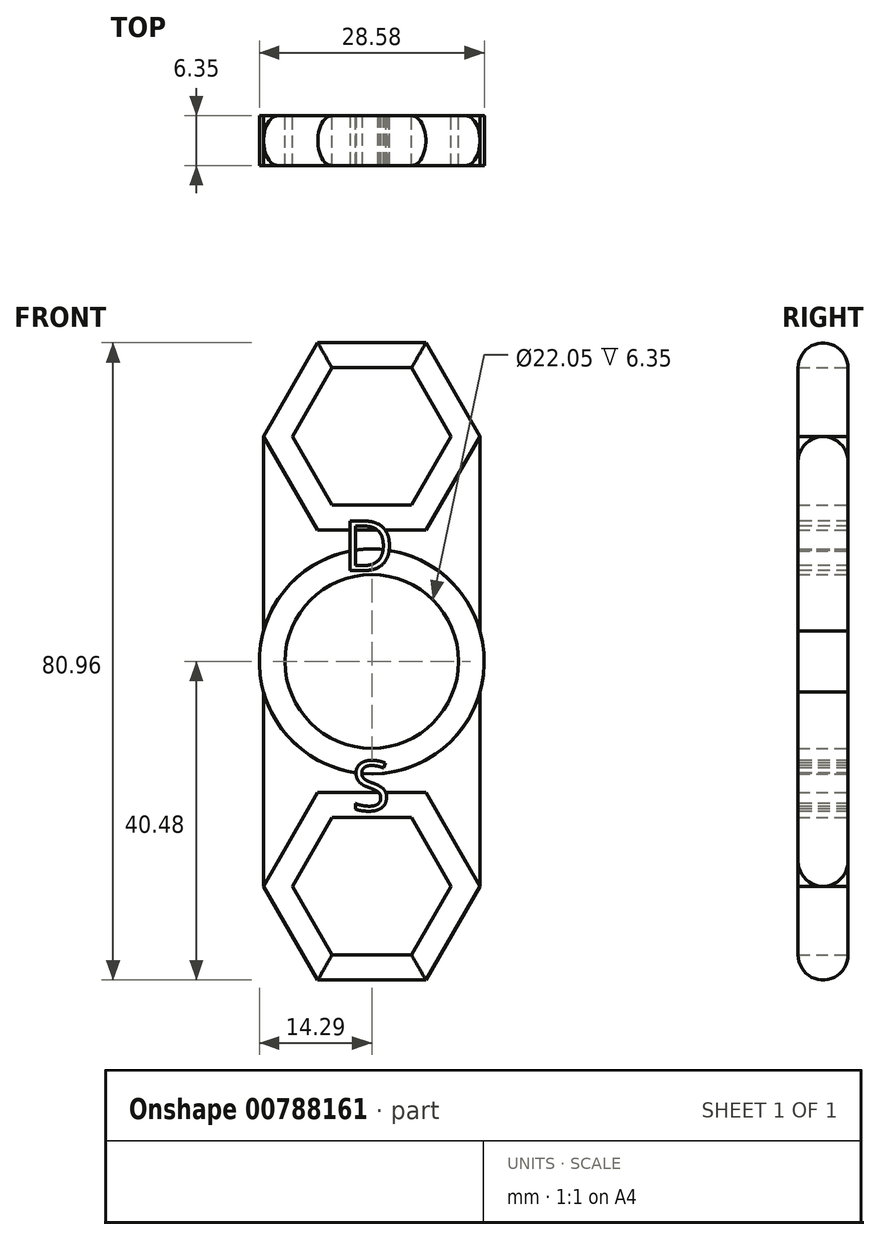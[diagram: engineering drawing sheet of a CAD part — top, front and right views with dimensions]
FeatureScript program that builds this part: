
annotation { "Feature Type Name" : "Feature", "Feature Type Description" : "" }
export const myFeature = defineFeature(function(context is Context, id is Id, definition is map)
    precondition{}
    {
        {
            var Q0;
            Q0=qCreatedBy(makeId("Front.planeOp"),FACE);
            var sketch = newSketch(context, id + "F0", { "sketchPlane" : qUnion([Q0])});
            skCircle(sketch, "E0", {"center": v(0, 0) * mm, "radius": 11.02 * mm});
            skCircle(sketch, "E1", {"center": v(0, 0) * mm, "radius": 14.29 * mm});
            skCircle(sketch, "E2.cCircle", {"center": v(0, 28.58) * mm, "radius": 8.73 * mm, "construction": true});
            skLineSegment(sketch, "E2.0", {"start": v(-5.04, 37.3) * mm, "end": v(5.04, 37.3) * mm});
            skLineSegment(sketch, "E2.1", {"start": v(5.04, 37.3) * mm, "end": v(10.08, 28.58) * mm});
            skLineSegment(sketch, "E2.2", {"start": v(10.08, 28.58) * mm, "end": v(5.04, 19.84) * mm});
            skLineSegment(sketch, "E2.3", {"start": v(5.04, 19.84) * mm, "end": v(-5.04, 19.84) * mm});
            skLineSegment(sketch, "E2.4", {"start": v(-5.04, 19.84) * mm, "end": v(-10.08, 28.58) * mm});
            skLineSegment(sketch, "E2.5", {"start": v(-10.08, 28.57) * mm, "end": v(-5.04, 37.3) * mm});
            skPoint(sketch, "E2.0.midPoint", {"position": v(0, 37.3) * mm});
            skCircle(sketch, "E3.cCircle", {"center": v(0, 28.58) * mm, "radius": 11.9 * mm, "construction": true});
            skLineSegment(sketch, "E3.0", {"start": v(-13.75, 28.58) * mm, "end": v(-6.87, 40.48) * mm});
            skLineSegment(sketch, "E3.1", {"start": v(-6.87, 40.48) * mm, "end": v(6.87, 40.48) * mm});
            skLineSegment(sketch, "E3.2", {"start": v(6.87, 40.48) * mm, "end": v(13.75, 28.58) * mm});
            skLineSegment(sketch, "E3.3", {"start": v(13.75, 28.58) * mm, "end": v(6.87, 16.67) * mm});
            skLineSegment(sketch, "E3.4", {"start": v(6.87, 16.67) * mm, "end": v(-6.87, 16.67) * mm});
            skLineSegment(sketch, "E3.5", {"start": v(-6.87, 16.67) * mm, "end": v(-13.75, 28.58) * mm});
            skPoint(sketch, "E3.0.midPoint", {"position": v(-10.31, 34.53) * mm});
            skCircle(sketch, "E4.1.0", {"center": v(0, -28.58) * mm, "radius": 11.9 * mm, "construction": true});
            skPoint(sketch, "E4.1.1", {"position": v(0, -37.3) * mm});
            skCircle(sketch, "E4.1.2", {"center": v(0, -28.58) * mm, "radius": 8.73 * mm, "construction": true});
            skPoint(sketch, "E4.1.3", {"position": v(10.31, -34.53) * mm});
            skLineSegment(sketch, "E4.1.4", {"start": v(-6.87, -16.67) * mm, "end": v(6.87, -16.67) * mm});
            skLineSegment(sketch, "E4.1.5", {"start": v(-5.04, -19.84) * mm, "end": v(5.04, -19.84) * mm});
            skLineSegment(sketch, "E4.1.6", {"start": v(-10.08, -28.58) * mm, "end": v(-5.04, -19.84) * mm});
            skLineSegment(sketch, "E4.1.7", {"start": v(5.04, -19.84) * mm, "end": v(10.08, -28.58) * mm});
            skLineSegment(sketch, "E4.1.8", {"start": v(10.08, -28.57) * mm, "end": v(5.04, -37.3) * mm});
            skLineSegment(sketch, "E4.1.9", {"start": v(5.04, -37.3) * mm, "end": v(-5.04, -37.3) * mm});
            skLineSegment(sketch, "E4.1.10", {"start": v(13.75, -28.58) * mm, "end": v(6.87, -40.48) * mm});
            skLineSegment(sketch, "E4.1.11", {"start": v(6.87, -40.48) * mm, "end": v(-6.87, -40.48) * mm});
            skLineSegment(sketch, "E4.1.12", {"start": v(-6.87, -40.48) * mm, "end": v(-13.75, -28.57) * mm});
            skLineSegment(sketch, "E4.1.13", {"start": v(-5.04, -37.3) * mm, "end": v(-10.08, -28.57) * mm});
            skLineSegment(sketch, "E4.1.14", {"start": v(6.87, -16.67) * mm, "end": v(13.75, -28.58) * mm});
            skLineSegment(sketch, "E4.1.15", {"start": v(-13.75, -28.58) * mm, "end": v(-6.87, -16.67) * mm});
            skSolve(sketch);
        }
        {
            var Q0;
            Q0=qCreatedBy(makeId("Front.planeOp"),FACE);
            var sketch = newSketch(context, id + "F1", { "sketchPlane" : qUnion([Q0])});
            skLineSegment(sketch, "E5.0", {"start": v(13.75, 28.58) * mm, "end": v(6.87, 16.67) * mm});
            skLineSegment(sketch, "E5.1", {"start": v(-5.04, -19.84) * mm, "end": v(5.04, -19.84) * mm});
            skLineSegment(sketch, "E5.2", {"start": v(5.04, -19.84) * mm, "end": v(10.08, -28.58) * mm});
            skLineSegment(sketch, "E5.3", {"start": v(13.75, -28.58) * mm, "end": v(6.87, -40.48) * mm});
            skLineSegment(sketch, "E5.4", {"start": v(-6.87, -40.48) * mm, "end": v(-13.75, -28.57) * mm});
            skLineSegment(sketch, "E5.5", {"start": v(6.87, -16.67) * mm, "end": v(13.75, -28.58) * mm});
            skLineSegment(sketch, "E5.6", {"start": v(6.87, 16.67) * mm, "end": v(-6.87, 16.67) * mm});
            skCircle(sketch, "E5.7", {"center": v(0, -28.58) * mm, "radius": 8.73 * mm});
            skLineSegment(sketch, "E5.8", {"start": v(-6.87, 16.67) * mm, "end": v(-13.75, 28.58) * mm});
            skCircle(sketch, "E5.9", {"center": v(0, 0) * mm, "radius": 11.02 * mm});
            skCircle(sketch, "E5.10", {"center": v(0, 0) * mm, "radius": 14.29 * mm});
            skCircle(sketch, "E5.11", {"center": v(0, 28.58) * mm, "radius": 8.73 * mm});
            skLineSegment(sketch, "E5.12", {"start": v(5.04, 37.3) * mm, "end": v(10.08, 28.58) * mm});
            skLineSegment(sketch, "E5.13", {"start": v(10.08, 28.58) * mm, "end": v(5.04, 19.84) * mm});
            skLineSegment(sketch, "E5.14", {"start": v(5.04, 19.84) * mm, "end": v(-5.04, 19.84) * mm});
            skLineSegment(sketch, "E5.15", {"start": v(-5.04, 19.84) * mm, "end": v(-10.08, 28.58) * mm});
            skLineSegment(sketch, "E5.16", {"start": v(-10.08, 28.57) * mm, "end": v(-5.04, 37.3) * mm});
            skCircle(sketch, "E5.17", {"center": v(0, 28.58) * mm, "radius": 11.9 * mm});
            skLineSegment(sketch, "E5.18", {"start": v(-13.75, 28.58) * mm, "end": v(-6.87, 40.48) * mm});
            skLineSegment(sketch, "E5.19", {"start": v(-6.87, 40.48) * mm, "end": v(6.87, 40.48) * mm});
            skLineSegment(sketch, "E5.20", {"start": v(6.87, 40.48) * mm, "end": v(13.75, 28.58) * mm});
            skLineSegment(sketch, "E5.21", {"start": v(-5.04, -37.3) * mm, "end": v(-10.08, -28.58) * mm});
            skLineSegment(sketch, "E5.22", {"start": v(6.87, -40.48) * mm, "end": v(-6.87, -40.48) * mm});
            skLineSegment(sketch, "E5.23", {"start": v(10.08, -28.57) * mm, "end": v(5.04, -37.3) * mm});
            skLineSegment(sketch, "E5.24", {"start": v(-10.08, -28.58) * mm, "end": v(-5.04, -19.84) * mm});
            skLineSegment(sketch, "E5.25", {"start": v(-13.75, -28.58) * mm, "end": v(-6.87, -16.67) * mm});
            skLineSegment(sketch, "E5.26", {"start": v(-6.87, -16.67) * mm, "end": v(6.87, -16.67) * mm});
            skCircle(sketch, "E5.27", {"center": v(0, -28.58) * mm, "radius": 11.9 * mm});
            skLineSegment(sketch, "E5.28", {"start": v(-5.04, 37.3) * mm, "end": v(5.04, 37.3) * mm});
            skPoint(sketch, "E6.0", {"position": v(13.75, 28.58) * mm});
            skPoint(sketch, "E7.0", {"position": v(-13.75, 28.58) * mm});
            skPoint(sketch, "E8.0", {"position": v(-13.75, -28.57) * mm});
            skLineSegment(sketch, "E9", {"start": v(-13.75, 28.58) * mm, "end": v(-13.75, -28.57) * mm});
            skLineSegment(sketch, "E10", {"start": v(13.75, 28.58) * mm, "end": v(13.75, -28.58) * mm});
            skSolve(sketch);
        }
        {
            var Q0;
            {var subQ5=sQuery(id+"F1.wireOp",EDGE,"E5.5");var subQ12=sQuery(id+"F1.wireOp",EDGE,"E5.26");var subQ13=makeQuery(id+"F1.imprint","INTERSECT",VERTEX,{"derivedFrom":[subQ5,subQ12]});Q0=makeQuery(id+"F1.imprint","IMPRINT",FACE,{"disambiguationData":[TD([[makeQuery(id+"F1.imprint","IMPRINT",EDGE,{"disambiguationData":[TD([[subQ13,-1.0]])],"derivedFrom":subQ5}),1.0]])]});}
            var Q1;
            {var subQ1=sQuery(id+"F1.wireOp",EDGE,"E5.6");var subQ5=sQuery(id+"F1.wireOp",EDGE,"E5.0");var subQ6=makeQuery(id+"F1.imprint","INTERSECT",VERTEX,{"derivedFrom":[subQ5,subQ1]});Q1=makeQuery(id+"F1.imprint","IMPRINT",FACE,{"disambiguationData":[TD([[makeQuery(id+"F1.imprint","IMPRINT",EDGE,{"disambiguationData":[TD([[subQ6,1.0]])],"derivedFrom":subQ5}),1.0]])]});}
            var Q2;
            Q2=makeQuery(id+"F0.imprint","IMPRINT",FACE,{"disambiguationData":[TD([[makeQuery(id+"F0.imprint","IMPRINT",EDGE,{"derivedFrom":sQuery(id+"F0.wireOp",EDGE,"E0")}),-1.0]])]});
            var Q3;
            Q3=makeQuery(id+"F0.imprint","IMPRINT",FACE,{"disambiguationData":[TD([[makeQuery(id+"F0.imprint","IMPRINT",EDGE,{"derivedFrom":sQuery(id+"F0.wireOp",EDGE,"E4.1.4")}),-1.0]])]});
            var Q4;
            Q4=makeQuery(id+"F0.imprint","IMPRINT",FACE,{"disambiguationData":[TD([[makeQuery(id+"F0.imprint","IMPRINT",EDGE,{"derivedFrom":sQuery(id+"F0.wireOp",EDGE,"E2.0")}),1.0]])]});
            extrude(context, id + "F2", {"entities" : qUnion([Q0, Q1, Q2, Q3, Q4]), "depth" : 6.35 * mm, "offsetDistance" : 25.4 * mm});
        }
        {
            var Q0;
            Q0=makeQuery(id+"F2.opExtrude","CAP_EDGE",EDGE,{"disambiguationData":[OSD([sQuery(id+"F0.wireOp",EDGE,"E3.0")])],"isStart":false});
            var Q1;
            Q1=makeQuery(id+"F2.opExtrude","CAP_EDGE",EDGE,{"disambiguationData":[OSD([sQuery(id+"F0.wireOp",EDGE,"E3.1")])],"isStart":false});
            var Q2;
            Q2=makeQuery(id+"F2.opExtrude","CAP_EDGE",EDGE,{"disambiguationData":[OSD([sQuery(id+"F0.wireOp",EDGE,"E3.2")])],"isStart":false});
            var Q3;
            {var subQ0=sQuery(id+"F1.wireOp",EDGE,"E10");Q3=makeQuery(id+"F2.opExtrude","CAP_EDGE",EDGE,{"disambiguationData":[OSD([subQ0]),TDD([makeQuery(id+"F1.imprint","IMPRINT",EDGE,{"disambiguationData":[TD([[makeQuery(id+"F1.imprint","INTERSECT",VERTEX,{"disambiguationData":[OD(0.0)],"derivedFrom":[sQuery(id+"F1.wireOp",EDGE,"E5.10"),subQ0]}),1.0]])],"derivedFrom":subQ0})])],"isStart":false});}
            var Q4;
            {var subQ0=sQuery(id+"F1.wireOp",EDGE,"E10");Q4=makeQuery(id+"F2.opExtrude","CAP_EDGE",EDGE,{"disambiguationData":[OSD([subQ0]),TDD([makeQuery(id+"F1.imprint","IMPRINT",EDGE,{"disambiguationData":[TD([[makeQuery(id+"F1.imprint","INTERSECT",VERTEX,{"disambiguationData":[OD(1.0)],"derivedFrom":[sQuery(id+"F1.wireOp",EDGE,"E5.10"),subQ0]}),-1.0]])],"derivedFrom":subQ0})])],"isStart":false});}
            var Q5;
            Q5=makeQuery(id+"F2.opExtrude","CAP_EDGE",EDGE,{"disambiguationData":[OSD([sQuery(id+"F0.wireOp",EDGE,"E4.1.10")])],"isStart":false});
            var Q6;
            Q6=makeQuery(id+"F2.opExtrude","CAP_EDGE",EDGE,{"disambiguationData":[OSD([sQuery(id+"F0.wireOp",EDGE,"E4.1.11")])],"isStart":false});
            var Q7;
            Q7=makeQuery(id+"F2.opExtrude","CAP_EDGE",EDGE,{"disambiguationData":[OSD([sQuery(id+"F0.wireOp",EDGE,"E4.1.12")])],"isStart":false});
            var Q8;
            {var subQ0=sQuery(id+"F1.wireOp",EDGE,"E9");Q8=makeQuery(id+"F2.opExtrude","CAP_EDGE",EDGE,{"disambiguationData":[OSD([subQ0]),TDD([makeQuery(id+"F1.imprint","IMPRINT",EDGE,{"disambiguationData":[TD([[makeQuery(id+"F1.imprint","INTERSECT",VERTEX,{"disambiguationData":[OD(1.0)],"derivedFrom":[sQuery(id+"F1.wireOp",EDGE,"E5.10"),subQ0]}),-1.0]])],"derivedFrom":subQ0})])],"isStart":false});}
            var Q9;
            {var subQ0=sQuery(id+"F1.wireOp",EDGE,"E9");Q9=makeQuery(id+"F2.opExtrude","CAP_EDGE",EDGE,{"disambiguationData":[OSD([subQ0]),TDD([makeQuery(id+"F1.imprint","IMPRINT",EDGE,{"disambiguationData":[TD([[makeQuery(id+"F1.imprint","INTERSECT",VERTEX,{"disambiguationData":[OD(0.0)],"derivedFrom":[sQuery(id+"F1.wireOp",EDGE,"E5.10"),subQ0]}),1.0]])],"derivedFrom":subQ0})])],"isStart":false});}
            var Q10;
            Q10=makeQuery(id+"F2.opExtrude","CAP_EDGE",EDGE,{"disambiguationData":[OSD([sQuery(id+"F0.wireOp",EDGE,"E3.1")])],"isStart":true});
            var Q11;
            Q11=makeQuery(id+"F2.opExtrude","CAP_EDGE",EDGE,{"disambiguationData":[OSD([sQuery(id+"F0.wireOp",EDGE,"E3.2")])],"isStart":true});
            var Q12;
            {var subQ0=sQuery(id+"F1.wireOp",EDGE,"E10");Q12=makeQuery(id+"F2.opExtrude","CAP_EDGE",EDGE,{"disambiguationData":[OSD([subQ0]),TDD([makeQuery(id+"F1.imprint","IMPRINT",EDGE,{"disambiguationData":[TD([[makeQuery(id+"F1.imprint","INTERSECT",VERTEX,{"disambiguationData":[OD(0.0)],"derivedFrom":[sQuery(id+"F1.wireOp",EDGE,"E5.10"),subQ0]}),1.0]])],"derivedFrom":subQ0})])],"isStart":true});}
            var Q13;
            {var subQ0=sQuery(id+"F1.wireOp",EDGE,"E10");Q13=makeQuery(id+"F2.opExtrude","CAP_EDGE",EDGE,{"disambiguationData":[OSD([subQ0]),TDD([makeQuery(id+"F1.imprint","IMPRINT",EDGE,{"disambiguationData":[TD([[makeQuery(id+"F1.imprint","INTERSECT",VERTEX,{"disambiguationData":[OD(1.0)],"derivedFrom":[sQuery(id+"F1.wireOp",EDGE,"E5.10"),subQ0]}),-1.0]])],"derivedFrom":subQ0})])],"isStart":true});}
            var Q14;
            Q14=makeQuery(id+"F2.opExtrude","CAP_EDGE",EDGE,{"disambiguationData":[OSD([sQuery(id+"F0.wireOp",EDGE,"E4.1.10")])],"isStart":true});
            var Q15;
            Q15=makeQuery(id+"F2.opExtrude","CAP_EDGE",EDGE,{"disambiguationData":[OSD([sQuery(id+"F0.wireOp",EDGE,"E4.1.11")])],"isStart":true});
            var Q16;
            Q16=makeQuery(id+"F2.opExtrude","CAP_EDGE",EDGE,{"disambiguationData":[OSD([sQuery(id+"F0.wireOp",EDGE,"E4.1.12")])],"isStart":true});
            var Q17;
            {var subQ0=sQuery(id+"F1.wireOp",EDGE,"E9");Q17=makeQuery(id+"F2.opExtrude","CAP_EDGE",EDGE,{"disambiguationData":[OSD([subQ0]),TDD([makeQuery(id+"F1.imprint","IMPRINT",EDGE,{"disambiguationData":[TD([[makeQuery(id+"F1.imprint","INTERSECT",VERTEX,{"disambiguationData":[OD(1.0)],"derivedFrom":[sQuery(id+"F1.wireOp",EDGE,"E5.10"),subQ0]}),-1.0]])],"derivedFrom":subQ0})])],"isStart":true});}
            var Q18;
            {var subQ0=sQuery(id+"F1.wireOp",EDGE,"E9");Q18=makeQuery(id+"F2.opExtrude","CAP_EDGE",EDGE,{"disambiguationData":[OSD([subQ0]),TDD([makeQuery(id+"F1.imprint","IMPRINT",EDGE,{"disambiguationData":[TD([[makeQuery(id+"F1.imprint","INTERSECT",VERTEX,{"disambiguationData":[OD(0.0)],"derivedFrom":[sQuery(id+"F1.wireOp",EDGE,"E5.10"),subQ0]}),1.0]])],"derivedFrom":subQ0})])],"isStart":true});}
            var Q19;
            Q19=makeQuery(id+"F2.opExtrude","CAP_EDGE",EDGE,{"disambiguationData":[OSD([sQuery(id+"F0.wireOp",EDGE,"E3.0")])],"isStart":true});
            fillet(context, id + "F3", {"entities" : qUnion([Q0, Q1, Q2, Q3, Q4, Q5, Q6, Q7, Q8, Q9, Q10, Q11, Q12, Q13, Q14, Q15, Q16, Q17, Q18, Q19]), "radius" : 3.17 * mm, "tangentPropagation" : true, "allowEdgeOverflow" : false});
        }
        {
            var Q0;
            Q0=makeQuery(id+"F2.opExtrude","CAP_FACE",FACE,{"disambiguationData":[OSD([sQuery(id+"F1.wireOp",EDGE,"E5.0"),sQuery(id+"F1.wireOp",EDGE,"E5.6"),sQuery(id+"F1.wireOp",EDGE,"E5.8"),sQuery(id+"F1.wireOp",EDGE,"E5.10"),sQuery(id+"F1.wireOp",EDGE,"E9"),sQuery(id+"F1.wireOp",EDGE,"E10")])],"isStart":false});
            var sketch = newSketch(context, id + "F4", { "sketchPlane" : qUnion([Q0])});
            skText(sketch, "E11", { "text": "D", "fontName": "OpenSans-Regular.ttf"});
            const initialGuessF4  = {"E11": [-0.00365, 0.01153, 1, 0, 0.00635]};
            skSetInitialGuess(sketch, initialGuessF4);
            skSolve(sketch);
        }
        {
            var Q0;
            Q0=makeQuery(id+"F2.opExtrude","CAP_FACE",FACE,{"disambiguationData":[OSD([sQuery(id+"F1.wireOp",EDGE,"E5.5"),sQuery(id+"F1.wireOp",EDGE,"E5.10"),sQuery(id+"F1.wireOp",EDGE,"E5.25"),sQuery(id+"F1.wireOp",EDGE,"E5.26"),sQuery(id+"F1.wireOp",EDGE,"E9"),sQuery(id+"F1.wireOp",EDGE,"E10")])],"isStart":false});
            var sketch = newSketch(context, id + "F5", { "sketchPlane" : qUnion([Q0])});
            skText(sketch, "E12", { "text": "S", "fontName": "OpenSans-Regular.ttf"});
            const initialGuessF5  = {"E12": [-0.00254, -0.01895, 1, 0, 0.00635]};
            skSetInitialGuess(sketch, initialGuessF5);
            skSolve(sketch);
        }
        {
            var Q0;
            {var subQ10=sQuery(id+"F4.wireOp",EDGE,"E11.sketch_text.stroke-4");Q0=makeQuery(id+"F4.imprint","IMPRINT",FACE,{"disambiguationData":[TD([[makeQuery(id+"F4.imprint","IMPRINT",EDGE,{"derivedFrom":subQ10}),-1.0]])]});}
            var Q1;
            {var subQ0=sQuery(id+"F4.wireOp",EDGE,"E11.sketch_text.stroke-3");var subQ4=makeQuery(id+"F2.opExtrude","CAP_EDGE",EDGE,{"disambiguationData":[OSD([sQuery(id+"F1.wireOp",EDGE,"E5.6")])],"isStart":false});var subQ5=makeQuery(id+"F4.imprint","INTERSECT",VERTEX,{"derivedFrom":[subQ4,subQ0]});Q1=makeQuery(id+"F4.imprint","IMPRINT",FACE,{"disambiguationData":[TD([[makeQuery(id+"F4.imprint","IMPRINT",EDGE,{"disambiguationData":[TD([[subQ5,1.0]])],"derivedFrom":subQ4}),1.0]])]});}
            var Q2;
            {var subQ5=sQuery(id+"F4.wireOp",EDGE,"E11.sketch_text.stroke-1");Q2=makeQuery(id+"F4.imprint","IMPRINT",FACE,{"disambiguationData":[TD([[makeQuery(id+"F4.imprint","IMPRINT",EDGE,{"derivedFrom":subQ5}),-1.0]])]});}
            var Q3;
            {var subQ1=sQuery(id+"F4.wireOp",EDGE,"E11.sketch_text.stroke-7");Q3=makeQuery(id+"F4.imprint","IMPRINT",FACE,{"disambiguationData":[TD([[makeQuery(id+"F4.imprint","IMPRINT",EDGE,{"derivedFrom":subQ1}),-1.0]])]});}
            extrude(context, id + "F6", {"entities" : qUnion([Q0, Q1, Q2, Q3]), "operationType" : NewBodyOperationType.REMOVE, "oppositeDirection" : true, "depth" : 25.4 * mm, "offsetDistance" : 25.4 * mm});
        }
        {
            var Q0;
            {var subQ0=sQuery(id+"F5.wireOp",EDGE,"E12.sketch_text.stroke-14");Q0=makeQuery(id+"F5.imprint","IMPRINT",FACE,{"disambiguationData":[TD([[makeQuery(id+"F5.imprint","IMPRINT",EDGE,{"derivedFrom":subQ0}),-1.0]])]});}
            var Q1;
            {var subQ9=sQuery(id+"F5.wireOp",EDGE,"E12.sketch_text.stroke-10");Q1=makeQuery(id+"F5.imprint","IMPRINT",FACE,{"disambiguationData":[TD([[makeQuery(id+"F5.imprint","IMPRINT",EDGE,{"derivedFrom":subQ9}),-1.0]])]});}
            var Q2;
            {var subQ5=sQuery(id+"F5.wireOp",EDGE,"E12.sketch_text.stroke-0");Q2=makeQuery(id+"F5.imprint","IMPRINT",FACE,{"disambiguationData":[TD([[makeQuery(id+"F5.imprint","IMPRINT",EDGE,{"derivedFrom":subQ5}),-1.0]])]});}
            extrude(context, id + "F7", {"entities" : qUnion([Q0, Q1, Q2]), "operationType" : NewBodyOperationType.REMOVE, "oppositeDirection" : true, "depth" : 25.4 * mm, "offsetDistance" : 25.4 * mm});
        }
    });
